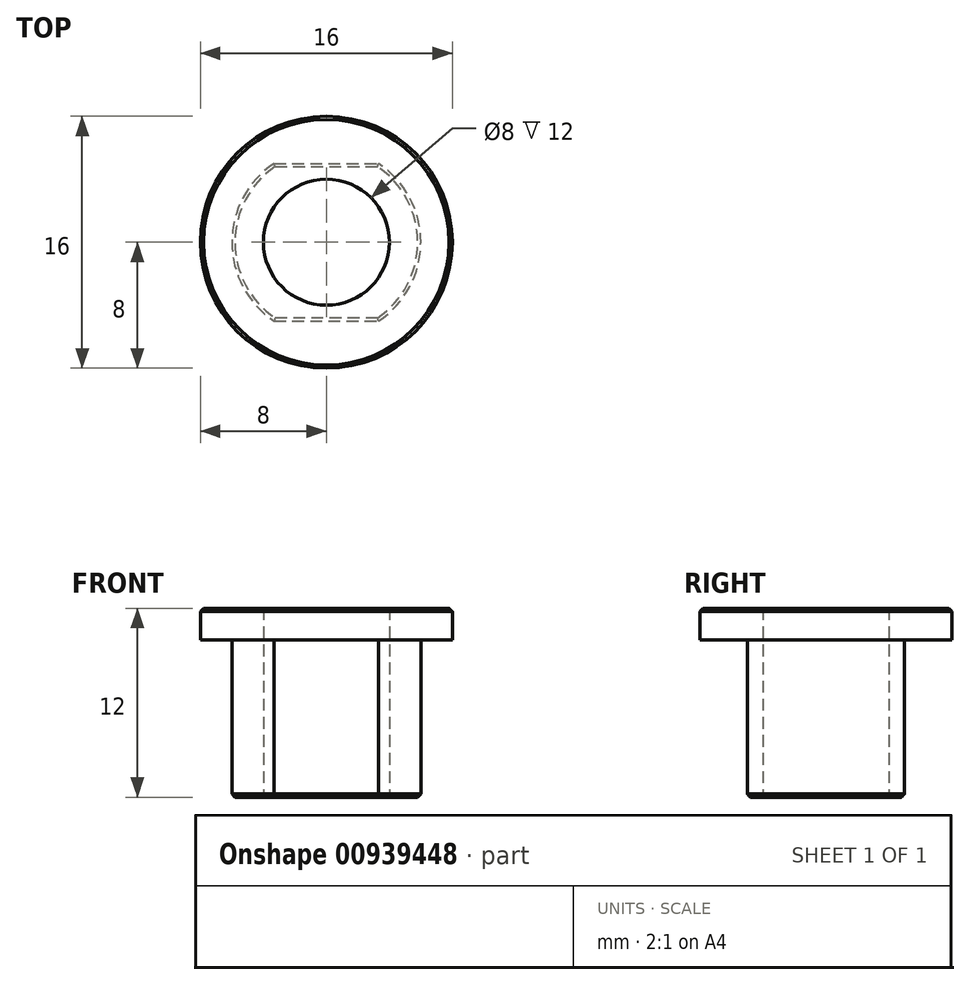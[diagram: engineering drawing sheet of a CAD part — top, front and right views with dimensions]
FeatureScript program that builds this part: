
annotation { "Feature Type Name" : "Feature", "Feature Type Description" : "" }
export const myFeature = defineFeature(function(context is Context, id is Id, definition is map)
    precondition{}
    {
        {
            var Q0;
            Q0=qCreatedBy(makeId("Top.planeOp"),FACE);
            var sketch = newSketch(context, id + "F0", { "sketchPlane" : qUnion([Q0])});
            skArc(sketch, "E0", {"start": v(-3.32, 5) * mm, "mid": v(-6, 0) * mm, "end": v(-3.32, -5) * mm});
            skCircle(sketch, "E1", {"center": v(0, 0) * mm, "radius": 4 * mm});
            skCircle(sketch, "E2", {"center": v(0, 0) * mm, "radius": 8 * mm});
            skLineSegment(sketch, "E3", {"start": v(-3.32, 5) * mm, "end": v(3.32, 5) * mm});
            skLineSegment(sketch, "E4", {"start": v(-3.32, -5) * mm, "end": v(3.32, -5) * mm});
            skArc(sketch, "E5.trimOffspring", {"start": v(3.32, -5) * mm, "mid": v(6, 0) * mm, "end": v(3.32, 5) * mm});
            skSolve(sketch);
        }
        {
            var Q0;
            Q0=makeQuery(id+"F0.imprint","IMPRINT",FACE,{"disambiguationData":[TD([[makeQuery(id+"F0.imprint","IMPRINT",EDGE,{"derivedFrom":sQuery(id+"F0.wireOp",EDGE,"E0")}),1.0]])]});
            var Q1;
            Q1=makeQuery(id+"F0.imprint","IMPRINT",FACE,{"disambiguationData":[TD([[makeQuery(id+"F0.imprint","IMPRINT",EDGE,{"derivedFrom":sQuery(id+"F0.wireOp",EDGE,"E0")}),-1.0]])]});
            extrude(context, id + "F1", {"entities" : qUnion([Q0, Q1]), "depth" : 2 * mm, "offsetDistance" : 25 * mm});
        }
        {
            var Q0;
            Q0=makeQuery(id+"F0.imprint","IMPRINT",FACE,{"disambiguationData":[TD([[makeQuery(id+"F0.imprint","IMPRINT",EDGE,{"derivedFrom":sQuery(id+"F0.wireOp",EDGE,"E0")}),1.0]])]});
            extrude(context, id + "F2", {"entities" : qUnion([Q0]), "operationType" : NewBodyOperationType.ADD, "oppositeDirection" : true, "depth" : 10 * mm, "offsetDistance" : 25 * mm});
        }
        {
            var Q0;
            Q0=makeQuery(id+"F1.opExtrude","CAP_EDGE",EDGE,{"disambiguationData":[OSD([sQuery(id+"F0.wireOp",EDGE,"E2")])],"isStart":false});
            var Q1;
            Q1=makeQuery(id+"F2.opExtrude","CAP_EDGE",EDGE,{"disambiguationData":[OSD([sQuery(id+"F0.wireOp",EDGE,"E0")])],"isStart":false});
            var Q2;
            Q2=makeQuery(id+"F2.opExtrude","CAP_EDGE",EDGE,{"disambiguationData":[OSD([sQuery(id+"F0.wireOp",EDGE,"E3")])],"isStart":false});
            var Q3;
            Q3=makeQuery(id+"F2.opExtrude","CAP_EDGE",EDGE,{"disambiguationData":[OSD([sQuery(id+"F0.wireOp",EDGE,"E5.trimOffspring")])],"isStart":false});
            var Q4;
            Q4=makeQuery(id+"F2.opExtrude","CAP_EDGE",EDGE,{"disambiguationData":[OSD([sQuery(id+"F0.wireOp",EDGE,"E4")])],"isStart":false});
            chamfer(context, id + "F3", {"entities" : qUnion([Q0, Q1, Q2, Q3, Q4]), "width" : 0.2 * mm, "tangentPropagation" : true});
        }
    });
